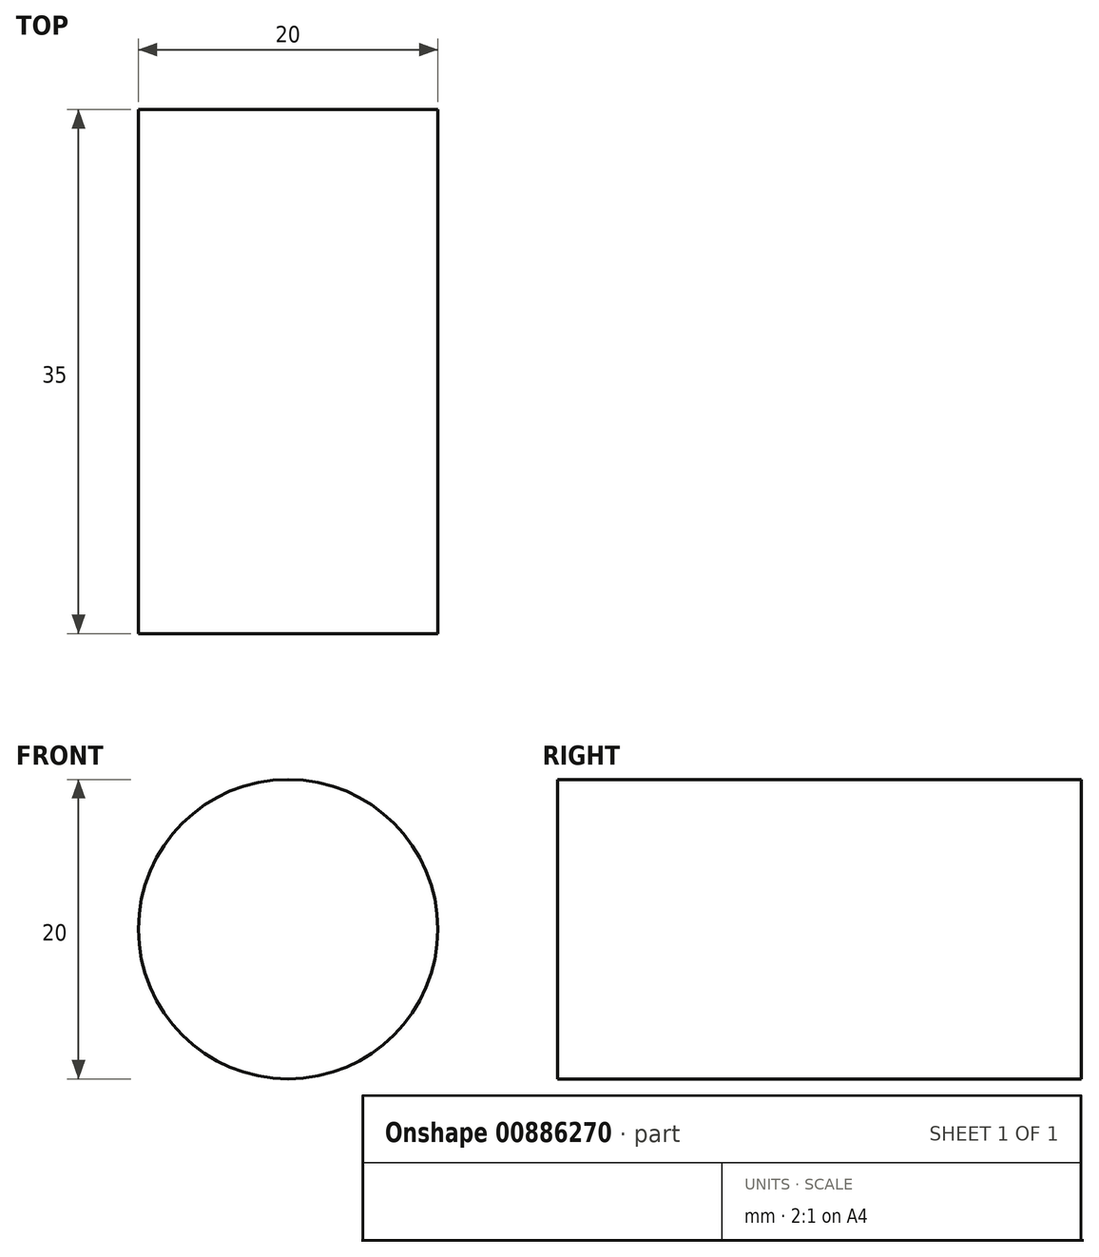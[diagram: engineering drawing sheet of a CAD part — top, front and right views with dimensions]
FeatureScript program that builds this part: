
annotation { "Feature Type Name" : "Feature", "Feature Type Description" : "" }
export const myFeature = defineFeature(function(context is Context, id is Id, definition is map)
    precondition{}
    {
        {
            var Q0;
            Q0=qCreatedBy(makeId("Front.planeOp"),FACE);
            var sketch = newSketch(context, id + "F0", { "sketchPlane" : qUnion([Q0])});
            skCircle(sketch, "E0", {"center": v(0, 0) * mm, "radius": 10 * mm});
            skSolve(sketch);
        }
        {
            var Q0;
            Q0 = qSketchRegion(id + "F0", true);
            extrude(context, id + "F1", {"entities" : qUnion([Q0]), "depth" : 35 * mm, "offsetDistance" : 25 * mm, "symmetric" : true});
        }
    });
